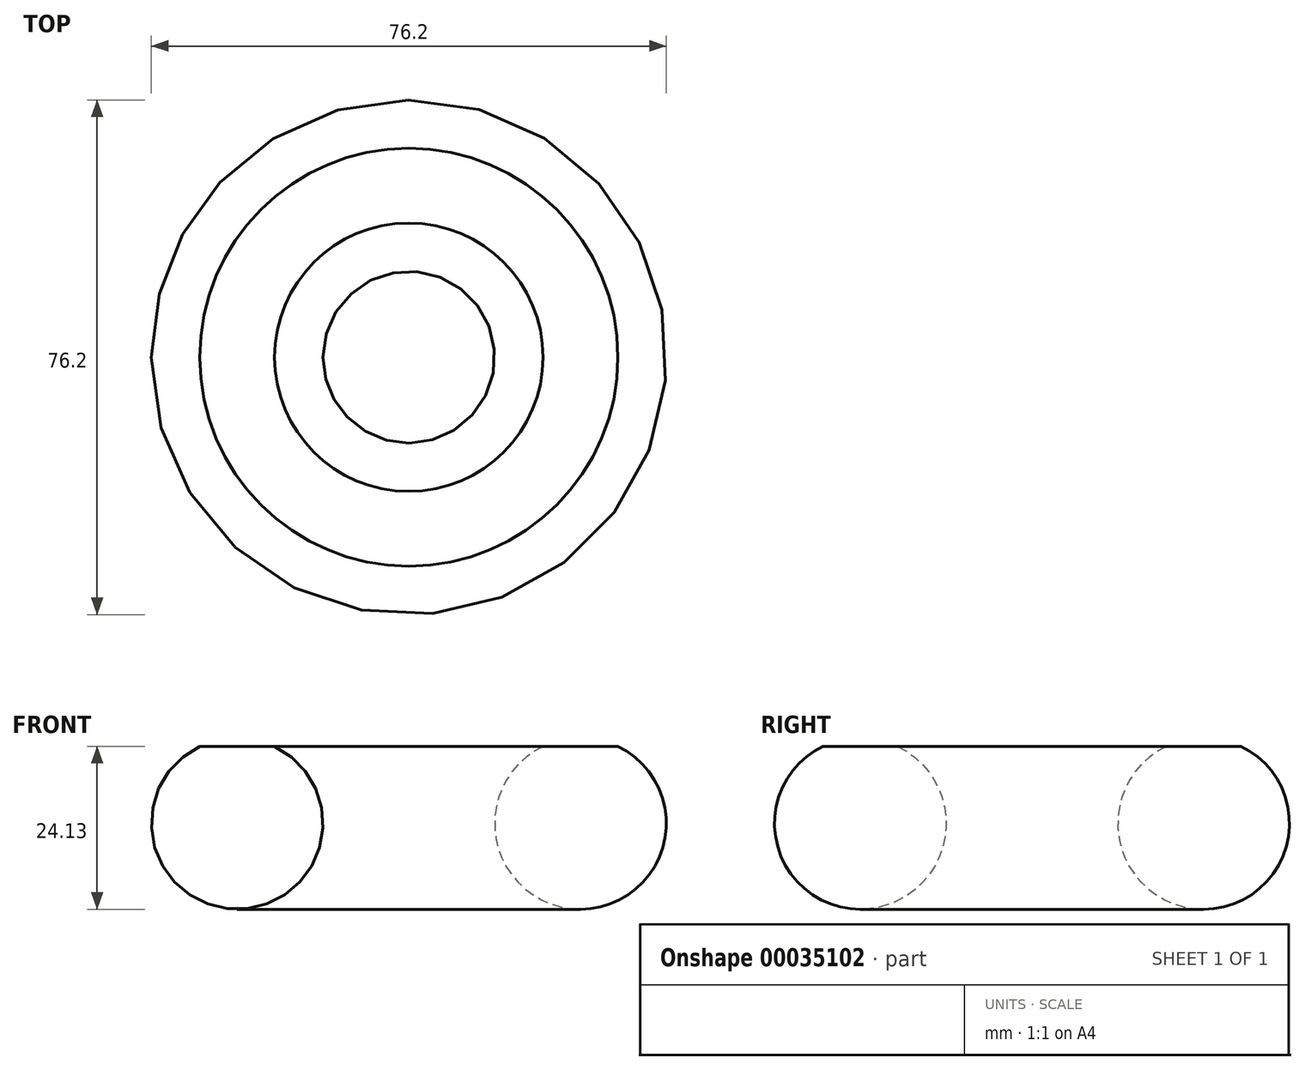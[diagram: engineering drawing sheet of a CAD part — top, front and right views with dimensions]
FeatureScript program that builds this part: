
annotation { "Feature Type Name" : "Feature", "Feature Type Description" : "" }
export const myFeature = defineFeature(function(context is Context, id is Id, definition is map)
    precondition{}
    {
        {
            var Q0;
            Q0=qCreatedBy(makeId("Front.planeOp"),FACE);
            var sketch = newSketch(context, id + "F0", { "sketchPlane" : qUnion([Q0])});
            skCircle(sketch, "E0", {"center": v(-25.4, 0) * mm, "radius": 12.7 * mm});
            skLineSegment(sketch, "E1", {"start": v(0, 0) * mm, "end": v(0, 45.92) * mm, "construction": true});
            skSolve(sketch);
        }
        {
            var Q0;
            Q0 = qSketchRegion(id + "F0", true);
            var Q1;
            Q1=sQuery(id+"F0.wireOp",EDGE,"E1");
            revolve(context, id + "F1", {"entities" : qUnion([Q0]), "axis" : qUnion([Q1]), "revolveType" : RevolveType.FULL});
        }
        {
            var Q0;
            Q0=qCreatedBy(makeId("Front.planeOp"),FACE);
            var sketch = newSketch(context, id + "F2", { "sketchPlane" : qUnion([Q0])});
            skLineSegment(sketch, "E2.bottom", {"start": v(-41.91, 24.13) * mm, "end": v(-10.16, 24.13) * mm});
            skLineSegment(sketch, "E2.top", {"start": v(-41.91, 11.43) * mm, "end": v(-10.16, 11.43) * mm});
            skLineSegment(sketch, "E2.left", {"start": v(-41.91, 24.13) * mm, "end": v(-41.91, 11.43) * mm});
            skLineSegment(sketch, "E2.right", {"start": v(-10.16, 24.13) * mm, "end": v(-10.16, 11.43) * mm});
            skLineSegment(sketch, "E3", {"start": v(0, 0) * mm, "end": v(0, 17.9) * mm});
            skPoint(sketch, "E4.orphan", {"position": v(0, 27.65) * mm});
            skSolve(sketch);
        }
        {
            var Q0;
            Q0 = qSketchRegion(id + "F2", true);
            var Q1;
            Q1=sQuery(id+"F2.wireOp",EDGE,"E3");
            revolve(context, id + "F3", {"operationType" : NewBodyOperationType.REMOVE, "entities" : qUnion([Q0]), "axis" : qUnion([Q1]), "revolveType" : RevolveType.FULL, "oppositeDirection" : true});
        }
    });
